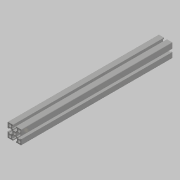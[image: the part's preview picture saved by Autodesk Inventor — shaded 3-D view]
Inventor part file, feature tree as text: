
AUTODESK INVENTOR PART (.ipt)
format: ipt  version: 2021.2 (Build 252289000, 289)  size: 199,680 bytes
history: native  units: in
note: dims shown in document units (in); Inventor stores cm internally (conversion verified against a paired STEP export)
features: other x2, extrude x1, sketch x1, projected_geometry x1
ambient origin geometry x8: Origin, YZ Plane, XZ Plane, XY Plane, X Axis, Y Axis, Z Axis, Center Point
bodies: Body1 (feature_tree)
feature tree (5):
  other  "ソリッド2"
  extrude  "押し出し1"  Depth=12.9921in
  sketch  "スケッチ2"
  projected_geometry  "投影ループ1"
  other  "ソリッド1"
